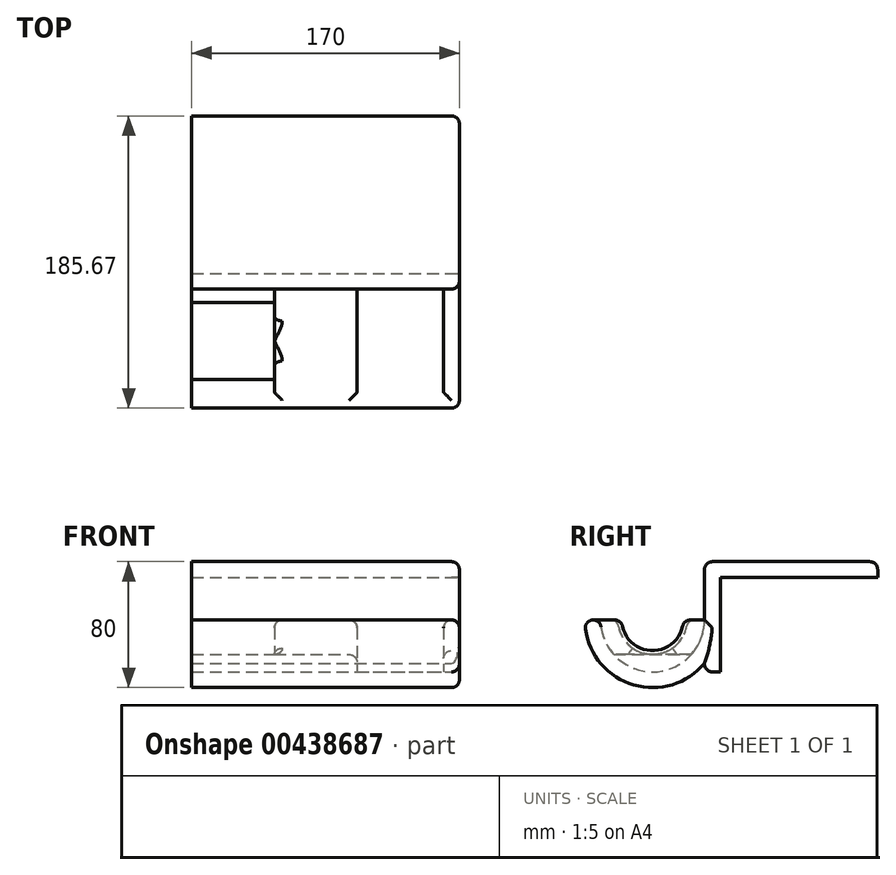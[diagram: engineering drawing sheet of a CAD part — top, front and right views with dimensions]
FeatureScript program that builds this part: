
annotation { "Feature Type Name" : "Feature", "Feature Type Description" : "" }
export const myFeature = defineFeature(function(context is Context, id is Id, definition is map)
    precondition{}
    {
        {
            var Q0;
            Q0=qCreatedBy(makeId("Front.planeOp"),FACE);
            var sketch = newSketch(context, id + "F0", { "sketchPlane" : qUnion([Q0])});
            skLineSegment(sketch, "E0.bottom", {"start": v(-170, 10) * mm, "end": v(170, 10) * mm});
            skLineSegment(sketch, "E0.top", {"start": v(-170, -60) * mm, "end": v(170, -60) * mm});
            skLineSegment(sketch, "E0.left", {"start": v(-170, 10) * mm, "end": v(-170, -60) * mm});
            skLineSegment(sketch, "E0.right", {"start": v(170, 10) * mm, "end": v(170, -60) * mm});
            skSolve(sketch);
        }
        {
            var Q0;
            Q0=qSketchRegion(id+"F0",true);
            extrude(context, id + "F1", {"entities" : qUnion([Q0]), "depth" : 10 * mm});
        }
        {
            var Q0;
            Q0=qCreatedBy(makeId("Top.planeOp"),FACE);
            var sketch = newSketch(context, id + "F2", { "sketchPlane" : qUnion([Q0])});
            skLineSegment(sketch, "E1.bottom", {"start": v(-170, 0) * mm, "end": v(170, 0) * mm});
            skLineSegment(sketch, "E1.top", {"start": v(-170, 100) * mm, "end": v(170, 100) * mm});
            skLineSegment(sketch, "E1.left", {"start": v(-170, 0) * mm, "end": v(-170, 100) * mm});
            skLineSegment(sketch, "E1.right", {"start": v(170, 0) * mm, "end": v(170, 100) * mm});
            skSolve(sketch);
        }
        {
            var Q0;
            Q0=qSketchRegion(id+"F2",true);
            extrude(context, id + "F3", {"entities" : qUnion([Q0]), "operationType" : NewBodyOperationType.ADD, "depth" : 10 * mm});
        }
        {
            var Q0;
            Q0=qCreatedBy(makeId("Top.planeOp"),FACE);
            cPlane(context, id + "F4", {"entities" : qUnion([Q0]), "cplaneType" : CPlaneType.OFFSET, "offset" : 27 * mm, "oppositeDirection" : true, "width" : 150 * mm, "height" : 150 * mm});
        }
        {
            var Q0;
            Q0=qCreatedBy(id+"F4.planeOp",FACE);
            var sketch = newSketch(context, id + "F5", { "sketchPlane" : qUnion([Q0])});
            skLineSegment(sketch, "E2", {"start": v(-170, 0) * mm, "end": v(-170, -43) * mm});
            skLineSegment(sketch, "E3", {"start": v(-170, -43) * mm, "end": v(-160, -43) * mm});
            skLineSegment(sketch, "E4", {"start": v(-160, -43) * mm, "end": v(-160, -10) * mm});
            skLineSegment(sketch, "E5", {"start": v(-160, -10) * mm, "end": v(-105, -10) * mm});
            skLineSegment(sketch, "E6", {"start": v(-105, -10) * mm, "end": v(-105, -21) * mm});
            skLineSegment(sketch, "E7", {"start": v(-105, -21) * mm, "end": v(-15, -21) * mm});
            skLineSegment(sketch, "E8", {"start": v(-15, -21) * mm, "end": v(-15, -10) * mm});
            skLineSegment(sketch, "E9", {"start": v(-15, -10) * mm, "end": v(52.5, -10) * mm});
            skLineSegment(sketch, "E10", {"start": v(52.5, -10) * mm, "end": v(52.5, -21) * mm});
            skLineSegment(sketch, "E11", {"start": v(52.5, -21) * mm, "end": v(105, -21) * mm});
            skLineSegment(sketch, "E12", {"start": v(105, -21) * mm, "end": v(105, -10) * mm});
            skLineSegment(sketch, "E13", {"start": v(105, -10) * mm, "end": v(160, -10) * mm});
            skLineSegment(sketch, "E14", {"start": v(160, -10) * mm, "end": v(160, -43) * mm});
            skLineSegment(sketch, "E15", {"start": v(160, -43) * mm, "end": v(170, -43) * mm});
            skLineSegment(sketch, "E16", {"start": v(170, -43) * mm, "end": v(170, 0) * mm});
            skLineSegment(sketch, "E17", {"start": v(170, 0) * mm, "end": v(-170, 0) * mm});
            skSolve(sketch);
        }
        {
            var Q0;
            Q0=qCreatedBy(id+"F4.planeOp",FACE);
            var sketch = newSketch(context, id + "F6", { "sketchPlane" : qUnion([Q0])});
            skLineSegment(sketch, "E18", {"start": v(170, -43) * mm, "end": v(-170, -43) * mm});
            skSolve(sketch);
        }
        {
            var Q0;
            Q0=qSketchRegion(id+"F5",true);
            var Q1;
            Q1=sQuery(id+"F6.wireOp",EDGE,"E18");
            revolve(context, id + "F7", {"operationType" : NewBodyOperationType.ADD, "entities" : qUnion([Q0]), "axis" : qUnion([Q1]), "revolveType" : RevolveType.ONE_DIRECTION, "angle" : 180 * degree});
        }
        {
            var Q0;
            Q0=qCreatedBy(makeId("Right.planeOp"),FACE);
            var sketch = newSketch(context, id + "F8", { "sketchPlane" : qUnion([Q0])});
            skCircle(sketch, "E19", {"center": v(-43, -27) * mm, "radius": 19.5 * mm});
            skSolve(sketch);
        }
        {
            var Q0;
            Q0=makeQuery(id+"F8.imprint","IMPRINT",FACE,{"disambiguationData":[TD([[makeQuery(id+"F8.imprint","IMPRINT",EDGE,{"derivedFrom":sQuery(id+"F8.wireOp",EDGE,"E19")}),1.0]])]});
            extrude(context, id + "F9", {"entities" : qUnion([Q0]), "operationType" : NewBodyOperationType.REMOVE, "endBound" : BoundingType.THROUGH_ALL, "depth" : 25 * mm});
        }
        {
            var Q0;
            Q0=qSketchRegion(id+"F8",true);
            extrude(context, id + "F10", {"entities" : qUnion([Q0]), "operationType" : NewBodyOperationType.REMOVE, "endBound" : BoundingType.THROUGH_ALL, "oppositeDirection" : true, "depth" : 25 * mm});
        }
        {
            var Q0;
            Q0=qCreatedBy(id+"F4.planeOp",FACE);
            cPlane(context, id + "F11", {"entities" : qUnion([Q0]), "cplaneType" : CPlaneType.OFFSET, "offset" : 22 * mm, "oppositeDirection" : true, "width" : 150 * mm, "height" : 150 * mm});
        }
        {
            var Q0;
            Q0=qCreatedBy(id+"F11.planeOp",FACE);
            var sketch = newSketch(context, id + "F12", { "sketchPlane" : qUnion([Q0])});
            skLineSegment(sketch, "E20.bottom", {"start": v(-15, -10) * mm, "end": v(52.5, -10) * mm});
            skLineSegment(sketch, "E20.top", {"start": v(-15, -76) * mm, "end": v(52.5, -76) * mm});
            skLineSegment(sketch, "E20.left", {"start": v(-15, -10) * mm, "end": v(-15, -76) * mm});
            skLineSegment(sketch, "E20.right", {"start": v(52.5, -10) * mm, "end": v(52.5, -76) * mm});
            skSolve(sketch);
        }
        {
            var Q0;
            Q0=makeQuery(id+"F12.imprint","IMPRINT",FACE,{"disambiguationData":[TD([[makeQuery(id+"F12.imprint","IMPRINT",EDGE,{"derivedFrom":sQuery(id+"F12.wireOp",EDGE,"E20.bottom")}),-1.0]])]});
            extrude(context, id + "F13", {"entities" : qUnion([Q0]), "operationType" : NewBodyOperationType.ADD, "oppositeDirection" : true, "depth" : 25 * mm});
        }
        {
            var Q0;
            Q0=makeQuery(id+"F13.opExtrude","SWEPT_FACE",FACE,{"disambiguationData":[OSD([sQuery(id+"F12.wireOp",EDGE,"E20.right")])]});
            var sketch = newSketch(context, id + "F14", { "sketchPlane" : qUnion([Q0])});
            skLineSegment(sketch, "E21", {"start": v(-76, -54.57) * mm, "end": v(-76, -74) * mm});
            skLineSegment(sketch, "E22", {"start": v(-76, -74) * mm, "end": v(-10, -74) * mm});
            skLineSegment(sketch, "E23", {"start": v(-10, -74) * mm, "end": v(-10, -54.57) * mm});
            skArc(sketch, "E24", {"start": v(-76, -54.57) * mm, "mid": v(-43, -70) * mm, "end": v(-10, -54.57) * mm});
            skSolve(sketch);
        }
        {
            var Q0;
            Q0=qSketchRegion(id+"F14",true);
            extrude(context, id + "F15", {"entities" : qUnion([Q0]), "operationType" : NewBodyOperationType.REMOVE, "endBound" : BoundingType.THROUGH_ALL, "oppositeDirection" : true, "depth" : 25 * mm});
        }
        {
            var Q0;
            Q0=qCreatedBy(makeId("Front.planeOp"),FACE);
            var sketch = newSketch(context, id + "F16", { "sketchPlane" : qUnion([Q0])});
            skLineSegment(sketch, "E25.bottom", {"start": v(0, 73) * mm, "end": v(-200, 73) * mm});
            skLineSegment(sketch, "E25.top", {"start": v(0, -127) * mm, "end": v(-200, -127) * mm});
            skLineSegment(sketch, "E25.left", {"start": v(0, 73) * mm, "end": v(0, -127) * mm});
            skLineSegment(sketch, "E25.right", {"start": v(-200, 73) * mm, "end": v(-200, -127) * mm});
            skSolve(sketch);
        }
        {
            var Q0;
            Q0 = qSketchRegion(id + "F16", true);
            extrude(context, id + "F17", {"entities" : qUnion([Q0]), "operationType" : NewBodyOperationType.REMOVE, "endBound" : BoundingType.THROUGH_ALL, "oppositeDirection" : true, "depth" : 25 * mm});
        }
        {
            var Q0;
            Q0 = qSketchRegion(id + "F16", true);
            extrude(context, id + "F18", {"entities" : qUnion([Q0]), "operationType" : NewBodyOperationType.REMOVE, "endBound" : BoundingType.THROUGH_ALL, "depth" : 25 * mm});
        }
        {
            var Q0;
            Q0=makeQuery(id+"F7.opRevolve","CAP_EDGE",EDGE,{"disambiguationData":[OSD([sQuery(id+"F5.wireOp",EDGE,"E17")])],"isStart":false});
            var Q1;
            Q1=makeQuery(id+"F7.opRevolve","CAP_EDGE",EDGE,{"disambiguationData":[OSD([sQuery(id+"F5.wireOp",EDGE,"E13")])],"isStart":false});
            var Q2;
            Q2=makeQuery(id+"F7.opRevolve","CAP_EDGE",EDGE,{"disambiguationData":[OSD([sQuery(id+"F5.wireOp",EDGE,"E9")])],"isStart":false});
            var Q3;
            Q3=makeQuery(id+"F7.opRevolve","CAP_EDGE",EDGE,{"disambiguationData":[OSD([sQuery(id+"F5.wireOp",EDGE,"E11")])],"isStart":false});
            var Q4;
            Q4=makeQuery(id+"F7.opRevolve","CAP_EDGE",EDGE,{"disambiguationData":[OSD([sQuery(id+"F5.wireOp",EDGE,"E12")])],"isStart":false});
            var Q5;
            Q5=makeQuery(id+"F7.opRevolve","CAP_EDGE",EDGE,{"disambiguationData":[OSD([sQuery(id+"F5.wireOp",EDGE,"E10")])],"isStart":false});
            var Q6;
            Q6=makeQuery(id+"F7.opRevolve","CAP_EDGE",EDGE,{"disambiguationData":[OSD([sQuery(id+"F5.wireOp",EDGE,"E11")])],"isStart":true});
            var Q7;
            Q7=makeQuery(id+"F7.opRevolve","CAP_EDGE",EDGE,{"disambiguationData":[OSD([sQuery(id+"F5.wireOp",EDGE,"E10")])],"isStart":true});
            var Q8;
            Q8=makeQuery(id+"F7.opRevolve","CAP_EDGE",EDGE,{"disambiguationData":[OSD([sQuery(id+"F5.wireOp",EDGE,"E12")])],"isStart":true});
            var Q9;
            {var subQ0=sQuery(id+"F5.wireOp",EDGE,"E14");var subQ1=sQuery(id+"F5.wireOp",EDGE,"E13");Q9=makeQuery(id+"F9.boolean.opBoolean","SPLIT",EDGE,{"disambiguationData":[TD([makeQuery(id+"F1.opExtrude","CAP_FACE",FACE,{"disambiguationData":[OSD([sQuery(id+"F0.wireOp",EDGE,"E0.bottom"),sQuery(id+"F0.wireOp",EDGE,"E0.top"),sQuery(id+"F0.wireOp",EDGE,"E0.left"),sQuery(id+"F0.wireOp",EDGE,"E0.right")])],"isStart":false}),makeQuery(id+"F7.opRevolve","CAP_FACE",FACE,{"disambiguationData":[OSD([sQuery(id+"F5.wireOp",EDGE,"E2"),sQuery(id+"F5.wireOp",EDGE,"E3"),sQuery(id+"F5.wireOp",EDGE,"E4"),sQuery(id+"F5.wireOp",EDGE,"E5"),sQuery(id+"F5.wireOp",EDGE,"E6"),sQuery(id+"F5.wireOp",EDGE,"E7"),sQuery(id+"F5.wireOp",EDGE,"E8"),sQuery(id+"F5.wireOp",EDGE,"E9"),sQuery(id+"F5.wireOp",EDGE,"E10"),sQuery(id+"F5.wireOp",EDGE,"E11"),sQuery(id+"F5.wireOp",EDGE,"E12"),subQ1,subQ0,sQuery(id+"F5.wireOp",EDGE,"E15"),sQuery(id+"F5.wireOp",EDGE,"E16"),sQuery(id+"F5.wireOp",EDGE,"E17")])],"isStart":false}),makeQuery(id+"F7.opRevolve","SWEPT_FACE",FACE,{"disambiguationData":[OSD([subQ1])]}),makeQuery(id+"F7.opRevolve","SWEPT_FACE",FACE,{"disambiguationData":[OSD([subQ0])]}),makeQuery(id+"F9.opExtrude","SWEPT_FACE",FACE,{"disambiguationData":[OSD([sQuery(id+"F8.wireOp",EDGE,"E19")])]})])],"derivedFrom":makeQuery(id+"F7.opRevolve","CAP_EDGE",EDGE,{"disambiguationData":[OSD([subQ0])],"isStart":false})});}
            var Q10;
            {var subQ0=sQuery(id+"F5.wireOp",EDGE,"E14");var subQ1=sQuery(id+"F5.wireOp",EDGE,"E13");Q10=makeQuery(id+"F9.boolean.opBoolean","SPLIT",EDGE,{"disambiguationData":[TD([makeQuery(id+"F7.opRevolve","CAP_FACE",FACE,{"disambiguationData":[OSD([sQuery(id+"F5.wireOp",EDGE,"E2"),sQuery(id+"F5.wireOp",EDGE,"E3"),sQuery(id+"F5.wireOp",EDGE,"E4"),sQuery(id+"F5.wireOp",EDGE,"E5"),sQuery(id+"F5.wireOp",EDGE,"E6"),sQuery(id+"F5.wireOp",EDGE,"E7"),sQuery(id+"F5.wireOp",EDGE,"E8"),sQuery(id+"F5.wireOp",EDGE,"E9"),sQuery(id+"F5.wireOp",EDGE,"E10"),sQuery(id+"F5.wireOp",EDGE,"E11"),sQuery(id+"F5.wireOp",EDGE,"E12"),subQ1,subQ0,sQuery(id+"F5.wireOp",EDGE,"E15"),sQuery(id+"F5.wireOp",EDGE,"E16"),sQuery(id+"F5.wireOp",EDGE,"E17")])],"isStart":false}),makeQuery(id+"F7.opRevolve","SWEPT_FACE",FACE,{"disambiguationData":[OSD([subQ1])]}),makeQuery(id+"F7.opRevolve","SWEPT_FACE",FACE,{"disambiguationData":[OSD([subQ0])]}),makeQuery(id+"F9.opExtrude","SWEPT_FACE",FACE,{"disambiguationData":[OSD([sQuery(id+"F8.wireOp",EDGE,"E19")])]})])],"derivedFrom":makeQuery(id+"F7.opRevolve","CAP_EDGE",EDGE,{"disambiguationData":[OSD([subQ0])],"isStart":false})});}
            var Q11;
            {var subQ0=sQuery(id+"F5.wireOp",EDGE,"E7");var subQ1=sQuery(id+"F5.wireOp",EDGE,"E6");var subQ2=sQuery(id+"F5.wireOp",EDGE,"E2");var subQ3=sQuery(id+"F5.wireOp",EDGE,"E5");var subQ4=sQuery(id+"F0.wireOp",EDGE,"E0.right");var subQ5=sQuery(id+"F0.wireOp",EDGE,"E0.left");var subQ6=sQuery(id+"F5.wireOp",EDGE,"E16");var subQ7=sQuery(id+"F5.wireOp",EDGE,"E4");var subQ8=sQuery(id+"F5.wireOp",EDGE,"E8");var subQ9=sQuery(id+"F5.wireOp",EDGE,"E9");var subQ10=sQuery(id+"F5.wireOp",EDGE,"E10");var subQ11=sQuery(id+"F5.wireOp",EDGE,"E11");var subQ12=sQuery(id+"F5.wireOp",EDGE,"E12");var subQ13=sQuery(id+"F5.wireOp",EDGE,"E13");var subQ14=sQuery(id+"F5.wireOp",EDGE,"E14");var subQ15=sQuery(id+"F5.wireOp",EDGE,"E17");Q11=makeQuery(id+"F9.boolean.opBoolean","INTERSECT",EDGE,{"disambiguationData":[OD(0.0)],"derivedFrom":[makeQuery(id+"F7.boolean.opBoolean","SPLIT",FACE,{"disambiguationData":[TD([makeQuery(id+"F1.opExtrude","CAP_FACE",FACE,{"disambiguationData":[OSD([sQuery(id+"F0.wireOp",EDGE,"E0.bottom"),sQuery(id+"F0.wireOp",EDGE,"E0.top"),subQ5,subQ4])],"isStart":false}),makeQuery(id+"F1.opExtrude","SWEPT_FACE",FACE,{"disambiguationData":[OSD([subQ5])]}),makeQuery(id+"F1.opExtrude","SWEPT_FACE",FACE,{"disambiguationData":[OSD([subQ4])]}),makeQuery(id+"F3.opExtrude","SWEPT_FACE",FACE,{"disambiguationData":[OSD([sQuery(id+"F2.wireOp",EDGE,"E1.left")])]}),makeQuery(id+"F3.opExtrude","SWEPT_FACE",FACE,{"disambiguationData":[OSD([sQuery(id+"F2.wireOp",EDGE,"E1.right")])]}),makeQuery(id+"F7.opRevolve","SWEPT_FACE",FACE,{"disambiguationData":[OSD([subQ2])]}),makeQuery(id+"F7.opRevolve","SWEPT_FACE",FACE,{"disambiguationData":[OSD([subQ7])]}),makeQuery(id+"F7.opRevolve","SWEPT_FACE",FACE,{"disambiguationData":[OSD([subQ3])]}),makeQuery(id+"F7.opRevolve","SWEPT_FACE",FACE,{"disambiguationData":[OSD([subQ1])]}),makeQuery(id+"F7.opRevolve","SWEPT_FACE",FACE,{"disambiguationData":[OSD([subQ0])]}),makeQuery(id+"F7.opRevolve","SWEPT_FACE",FACE,{"disambiguationData":[OSD([subQ8])]}),makeQuery(id+"F7.opRevolve","SWEPT_FACE",FACE,{"disambiguationData":[OSD([subQ9])]}),makeQuery(id+"F7.opRevolve","SWEPT_FACE",FACE,{"disambiguationData":[OSD([subQ10])]}),makeQuery(id+"F7.opRevolve","SWEPT_FACE",FACE,{"disambiguationData":[OSD([subQ11])]}),makeQuery(id+"F7.opRevolve","SWEPT_FACE",FACE,{"disambiguationData":[OSD([subQ12])]}),makeQuery(id+"F7.opRevolve","SWEPT_FACE",FACE,{"disambiguationData":[OSD([subQ13])]}),makeQuery(id+"F7.opRevolve","SWEPT_FACE",FACE,{"disambiguationData":[OSD([subQ14])]}),makeQuery(id+"F7.opRevolve","SWEPT_FACE",FACE,{"disambiguationData":[OSD([subQ6])]}),makeQuery(id+"F7.opRevolve","SWEPT_FACE",FACE,{"disambiguationData":[OSD([subQ15])]})])],"derivedFrom":makeQuery(id+"F7.opRevolve","CAP_FACE",FACE,{"disambiguationData":[OSD([subQ2,sQuery(id+"F5.wireOp",EDGE,"E3"),subQ7,subQ3,subQ1,subQ0,subQ8,subQ9,subQ10,subQ11,subQ12,subQ13,subQ14,sQuery(id+"F5.wireOp",EDGE,"E15"),subQ6,subQ15])],"isStart":false})}),makeQuery(id+"F9.opExtrude","SWEPT_FACE",FACE,{"disambiguationData":[OSD([sQuery(id+"F8.wireOp",EDGE,"E19")])]})]});}
            var Q12;
            {var subQ0=sQuery(id+"F5.wireOp",EDGE,"E7");var subQ1=sQuery(id+"F5.wireOp",EDGE,"E6");var subQ2=sQuery(id+"F5.wireOp",EDGE,"E2");var subQ3=sQuery(id+"F5.wireOp",EDGE,"E5");var subQ4=sQuery(id+"F0.wireOp",EDGE,"E0.right");var subQ5=sQuery(id+"F0.wireOp",EDGE,"E0.left");var subQ6=sQuery(id+"F5.wireOp",EDGE,"E16");var subQ7=sQuery(id+"F5.wireOp",EDGE,"E4");var subQ8=sQuery(id+"F5.wireOp",EDGE,"E8");var subQ9=sQuery(id+"F5.wireOp",EDGE,"E9");var subQ10=sQuery(id+"F5.wireOp",EDGE,"E10");var subQ11=sQuery(id+"F5.wireOp",EDGE,"E11");var subQ12=sQuery(id+"F5.wireOp",EDGE,"E12");var subQ13=sQuery(id+"F5.wireOp",EDGE,"E13");var subQ14=sQuery(id+"F5.wireOp",EDGE,"E14");var subQ15=sQuery(id+"F5.wireOp",EDGE,"E17");Q12=makeQuery(id+"F9.boolean.opBoolean","INTERSECT",EDGE,{"disambiguationData":[OD(1.0)],"derivedFrom":[makeQuery(id+"F7.boolean.opBoolean","SPLIT",FACE,{"disambiguationData":[TD([makeQuery(id+"F1.opExtrude","CAP_FACE",FACE,{"disambiguationData":[OSD([sQuery(id+"F0.wireOp",EDGE,"E0.bottom"),sQuery(id+"F0.wireOp",EDGE,"E0.top"),subQ5,subQ4])],"isStart":false}),makeQuery(id+"F1.opExtrude","SWEPT_FACE",FACE,{"disambiguationData":[OSD([subQ5])]}),makeQuery(id+"F1.opExtrude","SWEPT_FACE",FACE,{"disambiguationData":[OSD([subQ4])]}),makeQuery(id+"F3.opExtrude","SWEPT_FACE",FACE,{"disambiguationData":[OSD([sQuery(id+"F2.wireOp",EDGE,"E1.left")])]}),makeQuery(id+"F3.opExtrude","SWEPT_FACE",FACE,{"disambiguationData":[OSD([sQuery(id+"F2.wireOp",EDGE,"E1.right")])]}),makeQuery(id+"F7.opRevolve","SWEPT_FACE",FACE,{"disambiguationData":[OSD([subQ2])]}),makeQuery(id+"F7.opRevolve","SWEPT_FACE",FACE,{"disambiguationData":[OSD([subQ7])]}),makeQuery(id+"F7.opRevolve","SWEPT_FACE",FACE,{"disambiguationData":[OSD([subQ3])]}),makeQuery(id+"F7.opRevolve","SWEPT_FACE",FACE,{"disambiguationData":[OSD([subQ1])]}),makeQuery(id+"F7.opRevolve","SWEPT_FACE",FACE,{"disambiguationData":[OSD([subQ0])]}),makeQuery(id+"F7.opRevolve","SWEPT_FACE",FACE,{"disambiguationData":[OSD([subQ8])]}),makeQuery(id+"F7.opRevolve","SWEPT_FACE",FACE,{"disambiguationData":[OSD([subQ9])]}),makeQuery(id+"F7.opRevolve","SWEPT_FACE",FACE,{"disambiguationData":[OSD([subQ10])]}),makeQuery(id+"F7.opRevolve","SWEPT_FACE",FACE,{"disambiguationData":[OSD([subQ11])]}),makeQuery(id+"F7.opRevolve","SWEPT_FACE",FACE,{"disambiguationData":[OSD([subQ12])]}),makeQuery(id+"F7.opRevolve","SWEPT_FACE",FACE,{"disambiguationData":[OSD([subQ13])]}),makeQuery(id+"F7.opRevolve","SWEPT_FACE",FACE,{"disambiguationData":[OSD([subQ14])]}),makeQuery(id+"F7.opRevolve","SWEPT_FACE",FACE,{"disambiguationData":[OSD([subQ6])]}),makeQuery(id+"F7.opRevolve","SWEPT_FACE",FACE,{"disambiguationData":[OSD([subQ15])]})])],"derivedFrom":makeQuery(id+"F7.opRevolve","CAP_FACE",FACE,{"disambiguationData":[OSD([subQ2,sQuery(id+"F5.wireOp",EDGE,"E3"),subQ7,subQ3,subQ1,subQ0,subQ8,subQ9,subQ10,subQ11,subQ12,subQ13,subQ14,sQuery(id+"F5.wireOp",EDGE,"E15"),subQ6,subQ15])],"isStart":false})}),makeQuery(id+"F9.opExtrude","SWEPT_FACE",FACE,{"disambiguationData":[OSD([sQuery(id+"F8.wireOp",EDGE,"E19")])]})]});}
            var Q13;
            Q13=makeQuery(id+"F9.boolean.opBoolean","INTERSECT",EDGE,{"derivedFrom":[makeQuery(id+"F7.boolean.opBoolean","MERGE",FACE,{"derivedFrom":[makeQuery(id+"F3.boolean.opBoolean","MERGE",FACE,{"derivedFrom":[makeQuery(id+"F1.opExtrude","SWEPT_FACE",FACE,{"disambiguationData":[OSD([sQuery(id+"F0.wireOp",EDGE,"E0.right")])]}),makeQuery(id+"F3.opExtrude","SWEPT_FACE",FACE,{"disambiguationData":[OSD([sQuery(id+"F2.wireOp",EDGE,"E1.right")])]})]}),makeQuery(id+"F7.opRevolve","SWEPT_FACE",FACE,{"disambiguationData":[OSD([sQuery(id+"F5.wireOp",EDGE,"E16")])]})]}),makeQuery(id+"F9.opExtrude","SWEPT_FACE",FACE,{"disambiguationData":[OSD([sQuery(id+"F8.wireOp",EDGE,"E19")])]})]});
            var Q14;
            Q14=makeQuery(id+"F7.opRevolve","SWEPT_EDGE",EDGE,{"disambiguationData":[OSD([sQuery(id+"F5.wireOp",EDGE,"E16"),sQuery(id+"F5.wireOp",EDGE,"E17")])]});
            var Q15;
            {var subQ0=sQuery(id+"F0.wireOp",EDGE,"E0.right");var subQ1=sQuery(id+"F0.wireOp",EDGE,"E0.top");Q15=makeQuery(id+"F7.boolean.opBoolean","SPLIT",EDGE,{"disambiguationData":[TD([makeQuery(id+"F1.opExtrude","SWEPT_FACE",FACE,{"disambiguationData":[OSD([subQ1])]})])],"derivedFrom":makeQuery(id+"F1.opExtrude","CAP_EDGE",EDGE,{"disambiguationData":[OSD([subQ0])],"isStart":false})});}
            var Q16;
            Q16=makeQuery(id+"F1.opExtrude","SWEPT_EDGE",EDGE,{"disambiguationData":[OSD([sQuery(id+"F0.wireOp",EDGE,"E0.top"),sQuery(id+"F0.wireOp",EDGE,"E0.right")])]});
            var Q17;
            {var subQ0=sQuery(id+"F0.wireOp",EDGE,"E0.top");var subQ1=makeQuery(id+"F1.opExtrude","SWEPT_FACE",FACE,{"disambiguationData":[OSD([subQ0])]});var subQ2=makeQuery(id+"F13.opExtrude","SWEPT_FACE",FACE,{"disambiguationData":[OSD([sQuery(id+"F12.wireOp",EDGE,"E20.bottom")])]});var subQ3=makeQuery(id+"F1.opExtrude","CAP_EDGE",EDGE,{"disambiguationData":[OSD([subQ0])],"isStart":false});var subQ4=sQuery(id+"F0.wireOp",EDGE,"E0.right");var subQ5=sQuery(id+"F0.wireOp",EDGE,"E0.left");var subQ6=makeQuery(id+"F1.opExtrude","CAP_FACE",FACE,{"disambiguationData":[OSD([sQuery(id+"F0.wireOp",EDGE,"E0.bottom"),subQ0,subQ5,subQ4])],"isStart":false});Q17=makeQuery(id+"F15.boolean.opBoolean","MERGE",EDGE,{"derivedFrom":[makeQuery(id+"F13.boolean.opBoolean","SPLIT",EDGE,{"disambiguationData":[topologyDisambiguationEdgeConnected([subQ6,subQ1]),TD([makeQuery(id+"F1.opExtrude","SWEPT_FACE",FACE,{"disambiguationData":[OSD([subQ5])]})])],"derivedFrom":subQ3}),makeQuery(id+"F13.boolean.opBoolean","SPLIT",EDGE,{"disambiguationData":[topologyDisambiguationEdgeConnected([subQ6,subQ1]),TD([makeQuery(id+"F1.opExtrude","SWEPT_FACE",FACE,{"disambiguationData":[OSD([subQ4])]})])],"derivedFrom":subQ3}),makeQuery(id+"F13.boolean.opBoolean","SPLIT",EDGE,{"disambiguationData":[topologyDisambiguationEdgeConnected([subQ1,subQ2])],"derivedFrom":subQ3})]});}
            var Q18;
            Q18=makeQuery(id+"F13.boolean.opBoolean","SPLIT",EDGE,{"disambiguationData":[OD(0.0)],"derivedFrom":makeQuery(id+"F7.opRevolve","SWEPT_EDGE",EDGE,{"disambiguationData":[OSD([sQuery(id+"F5.wireOp",EDGE,"E10"),sQuery(id+"F5.wireOp",EDGE,"E11")])]})});
            var Q19;
            Q19=makeQuery(id+"F7.opRevolve","SWEPT_EDGE",EDGE,{"disambiguationData":[OSD([sQuery(id+"F5.wireOp",EDGE,"E11"),sQuery(id+"F5.wireOp",EDGE,"E12")])]});
            var Q20;
            Q20=makeQuery(id+"F9.boolean.opBoolean","INTERSECT",EDGE,{"derivedFrom":[makeQuery(id+"F7.opRevolve","SWEPT_FACE",FACE,{"disambiguationData":[OSD([sQuery(id+"F5.wireOp",EDGE,"E14")])]}),makeQuery(id+"F9.opExtrude","SWEPT_FACE",FACE,{"disambiguationData":[OSD([sQuery(id+"F8.wireOp",EDGE,"E19")])]})]});
            var Q21;
            {var subQ0=sQuery(id+"F0.wireOp",EDGE,"E0.right");var subQ1=sQuery(id+"F0.wireOp",EDGE,"E0.bottom");Q21=makeQuery(id+"F7.boolean.opBoolean","SPLIT",EDGE,{"disambiguationData":[TD([makeQuery(id+"F1.opExtrude","SWEPT_FACE",FACE,{"disambiguationData":[OSD([subQ1])]})])],"derivedFrom":makeQuery(id+"F1.opExtrude","CAP_EDGE",EDGE,{"disambiguationData":[OSD([subQ0])],"isStart":false})});}
            var Q22;
            Q22=makeQuery(id+"F3.boolean.opBoolean","MERGE",EDGE,{"derivedFrom":[makeQuery(id+"F1.opExtrude","SWEPT_EDGE",EDGE,{"disambiguationData":[OSD([sQuery(id+"F0.wireOp",EDGE,"E0.bottom"),sQuery(id+"F0.wireOp",EDGE,"E0.right")])]}),makeQuery(id+"F3.opExtrude","CAP_EDGE",EDGE,{"disambiguationData":[OSD([sQuery(id+"F2.wireOp",EDGE,"E1.right")])],"isStart":false})]});
            var Q23;
            Q23=makeQuery(id+"F3.opExtrude","CAP_EDGE",EDGE,{"disambiguationData":[OSD([sQuery(id+"F2.wireOp",EDGE,"E1.top")])],"isStart":false});
            var Q24;
            Q24=makeQuery(id+"F1.opExtrude","CAP_EDGE",EDGE,{"disambiguationData":[OSD([sQuery(id+"F0.wireOp",EDGE,"E0.bottom")])],"isStart":false});
            var Q25;
            Q25=makeQuery(id+"F3.opExtrude","SWEPT_EDGE",EDGE,{"disambiguationData":[OSD([sQuery(id+"F2.wireOp",EDGE,"E1.top"),sQuery(id+"F2.wireOp",EDGE,"E1.right")])]});
            var Q26;
            {var subQ0=sQuery(id+"F5.wireOp",EDGE,"E16");var subQ1=sQuery(id+"F0.wireOp",EDGE,"E0.right");Q26=makeQuery(id+"F9.boolean.opBoolean","SPLIT",EDGE,{"disambiguationData":[TD([makeQuery(id+"F1.opExtrude","CAP_FACE",FACE,{"disambiguationData":[OSD([sQuery(id+"F0.wireOp",EDGE,"E0.bottom"),sQuery(id+"F0.wireOp",EDGE,"E0.top"),sQuery(id+"F0.wireOp",EDGE,"E0.left"),subQ1])],"isStart":false})])],"derivedFrom":makeQuery(id+"F7.opRevolve","CAP_EDGE",EDGE,{"disambiguationData":[OSD([subQ0])],"isStart":false})});}
            var Q27;
            {var subQ0=sQuery(id+"F5.wireOp",EDGE,"E16");var subQ1=sQuery(id+"F5.wireOp",EDGE,"E17");Q27=makeQuery(id+"F9.boolean.opBoolean","SPLIT",EDGE,{"disambiguationData":[TD([makeQuery(id+"F7.opRevolve","SWEPT_FACE",FACE,{"disambiguationData":[OSD([subQ1])]})])],"derivedFrom":makeQuery(id+"F7.opRevolve","CAP_EDGE",EDGE,{"disambiguationData":[OSD([subQ0])],"isStart":false})});}
            fillet(context, id + "F19", {"entities" : qUnion([Q0, Q1, Q2, Q3, Q4, Q5, Q6, Q7, Q8, Q9, Q10, Q11, Q12, Q13, Q14, Q15, Q16, Q17, Q18, Q19, Q20, Q21, Q22, Q23, Q24, Q25, Q26, Q27]), "radius" : 5 * mm, "tangentPropagation" : true, "allowEdgeOverflow" : false});
        }
    });
